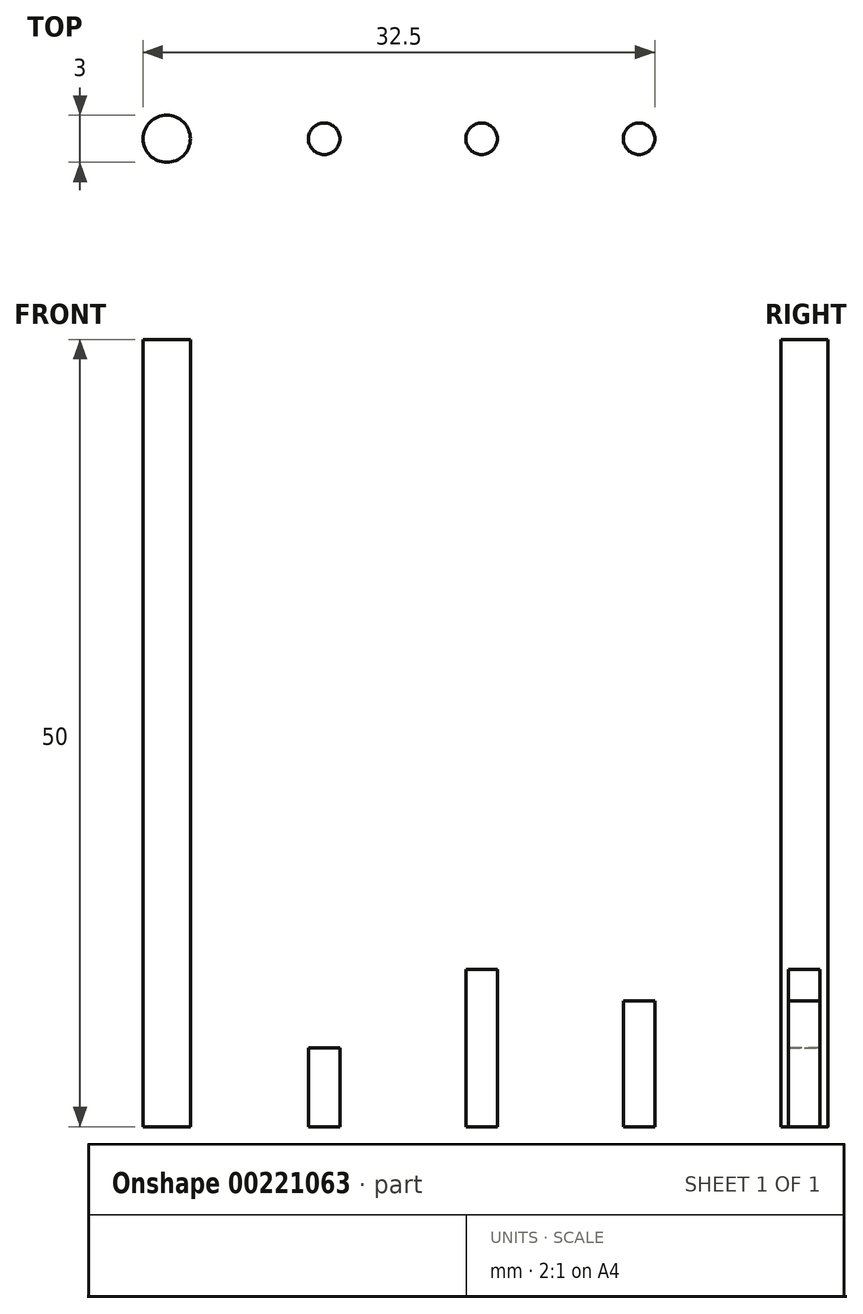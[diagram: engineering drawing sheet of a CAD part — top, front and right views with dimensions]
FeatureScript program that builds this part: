
annotation { "Feature Type Name" : "Feature", "Feature Type Description" : "" }
export const myFeature = defineFeature(function(context is Context, id is Id, definition is map)
    precondition{}
    {
        {
            var Q0;
            Q0=qCreatedBy(makeId("Top.planeOp"),FACE);
            var sketch = newSketch(context, id + "F0", { "sketchPlane" : qUnion([Q0])});
            skCircle(sketch, "E0", {"center": v(0, 0) * mm, "radius": 1 * mm});
            skSolve(sketch);
        }
        {
            var Q0;
            Q0=makeQuery(id+"F0.imprint","IMPRINT",FACE,{"disambiguationData":[TD([[makeQuery(id+"F0.imprint","IMPRINT",EDGE,{"derivedFrom":sQuery(id+"F0.wireOp",EDGE,"E0")}),1.0]])]});
            extrude(context, id + "F1", {"entities" : qUnion([Q0]), "depth" : 5 * mm});
        }
        {
            var Q0;
            Q0 = qSketchRegion(id + "F0", true);
            extrude(context, id + "F2", {"entities" : qUnion([Q0]), "depth" : 10 * mm});
        }
        {
            var Q0;
            Q0=makeQuery(id+"F2.opExtrude","SWEPT_BODY",BODY,{"disambiguationData":[OSD([sQuery(id+"F0.wireOp",EDGE,"E0")])]});
            transform(context, id + "F3", {"entities" : qUnion([Q0]), "transformType" : TransformType.TRANSLATION_3D, "dx" : 10 * mm, "dy" : 0 * mm, "dz" : 0 * mm, "makeCopy" : false});
        }
        {
            var Q0;
            Q0 = qSketchRegion(id + "F0", true);
            extrude(context, id + "F4", {"entities" : qUnion([Q0]), "depth" : 8 * mm});
        }
        {
            var Q0;
            Q0=makeQuery(id+"F4.opExtrude","SWEPT_BODY",BODY,{"disambiguationData":[OSD([sQuery(id+"F0.wireOp",EDGE,"E0")])]});
            transform(context, id + "F5", {"entities" : qUnion([Q0]), "transformType" : TransformType.TRANSLATION_3D, "dx" : 20 * mm, "dy" : 0 * mm, "dz" : 0 * mm, "makeCopy" : false});
        }
        {
            var Q0;
            Q0=qCreatedBy(makeId("Top.planeOp"),FACE);
            var sketch = newSketch(context, id + "F6", { "sketchPlane" : qUnion([Q0])});
            skCircle(sketch, "E1", {"center": v(-10, 0) * mm, "radius": 1.5 * mm});
            skSolve(sketch);
        }
        {
            var Q0;
            Q0=makeQuery(id+"F6.imprint","IMPRINT",FACE,{"disambiguationData":[TD([[makeQuery(id+"F6.imprint","IMPRINT",EDGE,{"derivedFrom":sQuery(id+"F6.wireOp",EDGE,"E1")}),1.0]])]});
            extrude(context, id + "F7", {"entities" : qUnion([Q0]), "depth" : 50 * mm});
        }
    });
